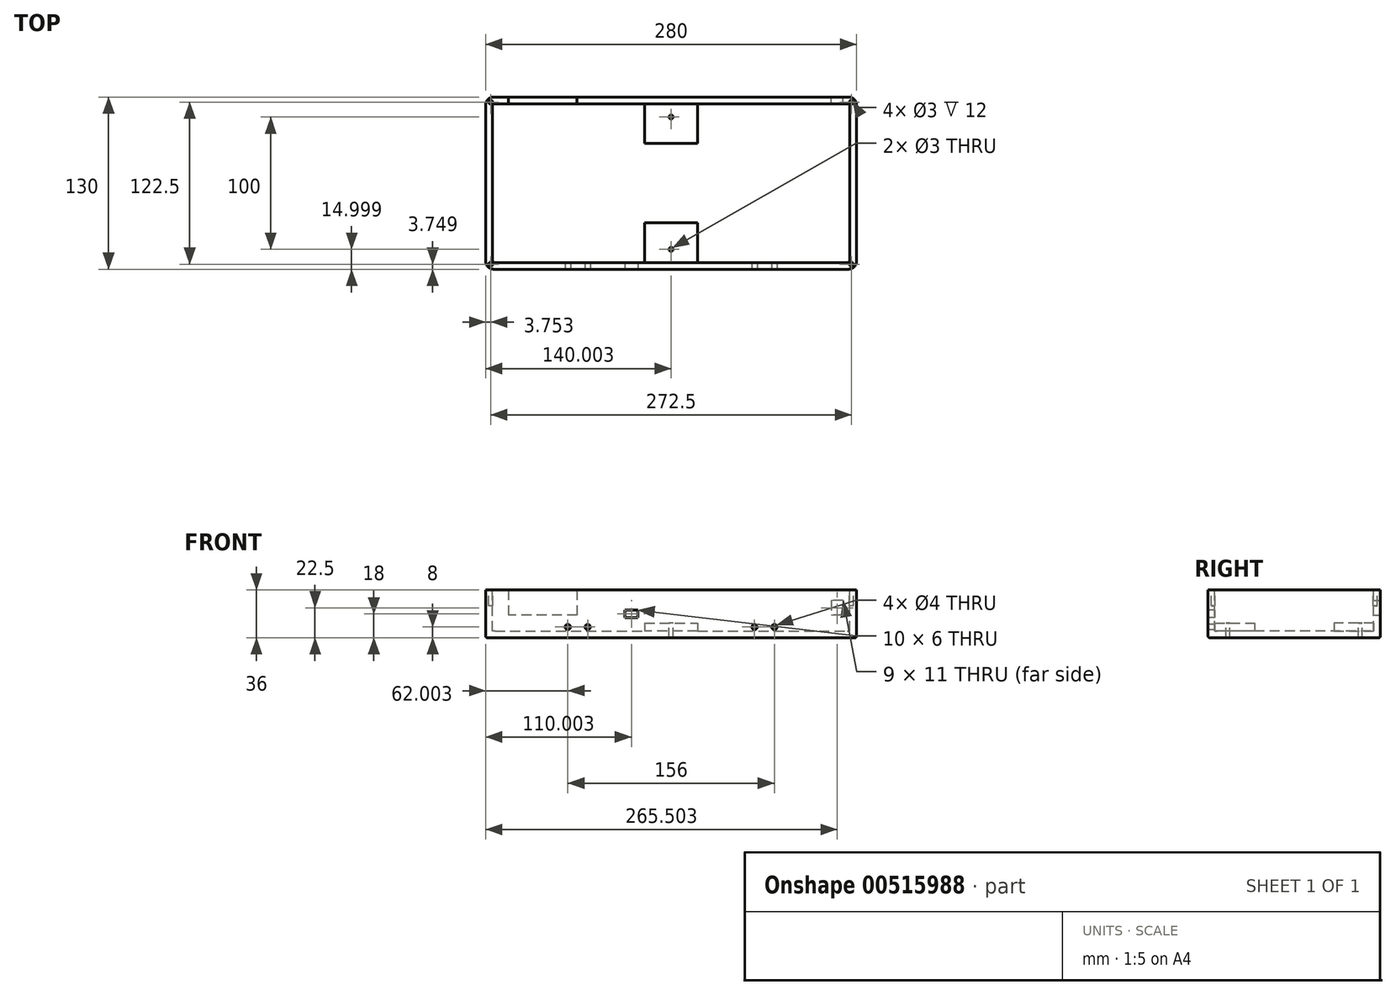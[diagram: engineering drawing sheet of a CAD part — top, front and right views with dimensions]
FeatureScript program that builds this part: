
annotation { "Feature Type Name" : "Feature", "Feature Type Description" : "" }
export const myFeature = defineFeature(function(context is Context, id is Id, definition is map)
    precondition{}
    {
        {
            var Q0;
            Q0=qCreatedBy(makeId("Top.planeOp"),FACE);
            var sketch = newSketch(context, id + "F0", { "sketchPlane" : qUnion([Q0])});
            skLineSegment(sketch, "E0.bottom", {"start": v(-152.6, 53.73) * mm, "end": v(127.4, 53.73) * mm});
            skLineSegment(sketch, "E0.top", {"start": v(-152.6, -76.27) * mm, "end": v(127.4, -76.27) * mm});
            skLineSegment(sketch, "E0.left", {"start": v(-152.6, 53.73) * mm, "end": v(-152.6, -76.27) * mm});
            skLineSegment(sketch, "E0.right", {"start": v(127.4, 53.73) * mm, "end": v(127.4, -76.27) * mm});
            skSolve(sketch);
        }
        {
            var Q0;
            Q0=makeQuery(id+"F0.imprint","IMPRINT",FACE,{"disambiguationData":[TD([[makeQuery(id+"F0.imprint","IMPRINT",EDGE,{"derivedFrom":sQuery(id+"F0.wireOp",EDGE,"E0.bottom")}),-1.0]])]});
            extrude(context, id + "F1", {"entities" : qUnion([Q0]), "depth" : 36 * mm, "offsetDistance" : 25 * mm});
        }
        {
            var Q0;
            Q0=makeQuery(id+"F1.opExtrude","CAP_FACE",FACE,{"disambiguationData":[OSD([sQuery(id+"F0.wireOp",EDGE,"E0.bottom"),sQuery(id+"F0.wireOp",EDGE,"E0.top"),sQuery(id+"F0.wireOp",EDGE,"E0.left"),sQuery(id+"F0.wireOp",EDGE,"E0.right")])],"isStart":false});
            var sketch = newSketch(context, id + "F2", { "sketchPlane" : qUnion([Q0])});
            skLineSegment(sketch, "E1.bottom", {"start": v(-147.6, 48.73) * mm, "end": v(122.4, 48.73) * mm});
            skLineSegment(sketch, "E1.top", {"start": v(-147.6, -71.27) * mm, "end": v(122.4, -71.27) * mm});
            skLineSegment(sketch, "E1.left", {"start": v(-147.6, 48.73) * mm, "end": v(-147.6, -71.27) * mm});
            skLineSegment(sketch, "E1.right", {"start": v(122.4, 48.73) * mm, "end": v(122.4, -71.27) * mm});
            skSolve(sketch);
        }
        {
            var Q0;
            Q0=makeQuery(id+"F2.imprint","IMPRINT",FACE,{"disambiguationData":[TD([[makeQuery(id+"F2.imprint","IMPRINT",EDGE,{"derivedFrom":sQuery(id+"F2.wireOp",EDGE,"E1.bottom")}),-1.0]])]});
            extrude(context, id + "F3", {"entities" : qUnion([Q0]), "operationType" : NewBodyOperationType.REMOVE, "oppositeDirection" : true, "depth" : 31 * mm, "offsetDistance" : 25 * mm});
        }
        {
            var Q0;
            Q0=makeQuery(id+"F1.opExtrude","SWEPT_FACE",FACE,{"disambiguationData":[OSD([sQuery(id+"F0.wireOp",EDGE,"E0.top")])]});
            var sketch = newSketch(context, id + "F4", { "sketchPlane" : qUnion([Q0])});
            skCircle(sketch, "E2", {"center": v(-90.6, 8) * mm, "radius": 2 * mm});
            skCircle(sketch, "E3", {"center": v(-75.6, 8) * mm, "radius": 2 * mm});
            skCircle(sketch, "E4", {"center": v(50.4, 8) * mm, "radius": 2 * mm});
            skCircle(sketch, "E5", {"center": v(65.4, 8) * mm, "radius": 2 * mm});
            skLineSegment(sketch, "E6.bottom", {"start": v(-47.6, 21) * mm, "end": v(-37.6, 21) * mm});
            skLineSegment(sketch, "E6.top", {"start": v(-47.6, 15) * mm, "end": v(-37.6, 15) * mm});
            skLineSegment(sketch, "E6.left", {"start": v(-47.6, 21) * mm, "end": v(-47.6, 15) * mm});
            skLineSegment(sketch, "E6.right", {"start": v(-37.6, 21) * mm, "end": v(-37.6, 15) * mm});
            skSolve(sketch);
        }
        {
            var Q0;
            Q0=makeQuery(id+"F1.opExtrude","SWEPT_FACE",FACE,{"disambiguationData":[OSD([sQuery(id+"F0.wireOp",EDGE,"E0.bottom")])]});
            var sketch = newSketch(context, id + "F5", { "sketchPlane" : qUnion([Q0])});
            skLineSegment(sketch, "E7.bottom", {"start": v(83.6, 36) * mm, "end": v(135.6, 36) * mm});
            skLineSegment(sketch, "E7.top", {"start": v(83.6, 17) * mm, "end": v(135.6, 17) * mm});
            skLineSegment(sketch, "E7.left", {"start": v(83.6, 36) * mm, "end": v(83.6, 17) * mm});
            skLineSegment(sketch, "E7.right", {"start": v(135.6, 36) * mm, "end": v(135.6, 17) * mm});
            skLineSegment(sketch, "E8.bottom", {"start": v(-117.4, 28) * mm, "end": v(-108.4, 28) * mm});
            skLineSegment(sketch, "E8.top", {"start": v(-117.4, 17) * mm, "end": v(-108.4, 17) * mm});
            skLineSegment(sketch, "E8.left", {"start": v(-117.4, 28) * mm, "end": v(-117.4, 17) * mm});
            skLineSegment(sketch, "E8.right", {"start": v(-108.4, 28) * mm, "end": v(-108.4, 17) * mm});
            skSolve(sketch);
        }
        {
            var Q0;
            Q0=makeQuery(id+"F4.imprint","IMPRINT",FACE,{"disambiguationData":[TD([[makeQuery(id+"F4.imprint","IMPRINT",EDGE,{"derivedFrom":sQuery(id+"F4.wireOp",EDGE,"E2")}),1.0]])]});
            var Q1;
            Q1=makeQuery(id+"F4.imprint","IMPRINT",FACE,{"disambiguationData":[TD([[makeQuery(id+"F4.imprint","IMPRINT",EDGE,{"derivedFrom":sQuery(id+"F4.wireOp",EDGE,"E3")}),1.0]])]});
            var Q2;
            Q2=makeQuery(id+"F4.imprint","IMPRINT",FACE,{"disambiguationData":[TD([[makeQuery(id+"F4.imprint","IMPRINT",EDGE,{"derivedFrom":sQuery(id+"F4.wireOp",EDGE,"E4")}),1.0]])]});
            var Q3;
            Q3=makeQuery(id+"F4.imprint","IMPRINT",FACE,{"disambiguationData":[TD([[makeQuery(id+"F4.imprint","IMPRINT",EDGE,{"derivedFrom":sQuery(id+"F4.wireOp",EDGE,"E5")}),1.0]])]});
            var Q4;
            Q4=makeQuery(id+"F4.imprint","IMPRINT",FACE,{"disambiguationData":[TD([[makeQuery(id+"F4.imprint","IMPRINT",EDGE,{"derivedFrom":sQuery(id+"F4.wireOp",EDGE,"EG82mpZ8-gIm3-i3lA-bKAT-wHgxzZ3Zt91a")}),1.0]])]});
            var Q5;
            Q5=makeQuery(id+"F4.imprint","IMPRINT",FACE,{"disambiguationData":[TD([[makeQuery(id+"F4.imprint","IMPRINT",EDGE,{"derivedFrom":sQuery(id+"F4.wireOp",EDGE,"E6.bottom")}),-1.0]])]});
            extrude(context, id + "F6", {"entities" : qUnion([Q0, Q1, Q2, Q3, Q4, Q5]), "operationType" : NewBodyOperationType.REMOVE, "oppositeDirection" : true, "depth" : 25 * mm, "offsetDistance" : 25 * mm});
        }
        {
            var Q0;
            Q0=makeQuery(id+"F5.imprint","IMPRINT",FACE,{"disambiguationData":[TD([[makeQuery(id+"F5.imprint","IMPRINT",EDGE,{"derivedFrom":sQuery(id+"F5.wireOp",EDGE,"E7.bottom")}),-1.0]])]});
            var Q1;
            Q1=makeQuery(id+"F5.imprint","IMPRINT",FACE,{"disambiguationData":[TD([[makeQuery(id+"F5.imprint","IMPRINT",EDGE,{"derivedFrom":sQuery(id+"F5.wireOp",EDGE,"E8.bottom")}),-1.0]])]});
            var Q2;
            Q2=makeQuery(id+"F5.imprint","IMPRINT",FACE,{"disambiguationData":[TD([[makeQuery(id+"F5.imprint","IMPRINT",EDGE,{"derivedFrom":sQuery(id+"F5.wireOp",EDGE,"E7.bottom")}),1.0]])]});
            extrude(context, id + "F7", {"entities" : qUnion([Q0, Q1, Q2]), "operationType" : NewBodyOperationType.REMOVE, "oppositeDirection" : true, "depth" : 25 * mm, "offsetDistance" : 25 * mm});
        }
        {
            var Q0;
            Q0=makeQuery(id+"F1.opExtrude","CAP_FACE",FACE,{"disambiguationData":[OSD([sQuery(id+"F0.wireOp",EDGE,"E0.bottom"),sQuery(id+"F0.wireOp",EDGE,"E0.top"),sQuery(id+"F0.wireOp",EDGE,"E0.left"),sQuery(id+"F0.wireOp",EDGE,"E0.right")])],"isStart":true});
            var sketch = newSketch(context, id + "F8", { "sketchPlane" : qUnion([Q0])});
            skLineSegment(sketch, "E9.bottom", {"start": v(-32.6, 71.27) * mm, "end": v(7.4, 71.27) * mm});
            skLineSegment(sketch, "E9.top", {"start": v(-32.6, 41.27) * mm, "end": v(7.4, 41.27) * mm});
            skLineSegment(sketch, "E9.left", {"start": v(-32.6, 71.27) * mm, "end": v(-32.6, 41.27) * mm});
            skLineSegment(sketch, "E9.right", {"start": v(7.4, 71.27) * mm, "end": v(7.4, 41.27) * mm});
            skLineSegment(sketch, "E10.bottom", {"start": v(-32.6, -48.73) * mm, "end": v(7.4, -48.73) * mm});
            skLineSegment(sketch, "E10.top", {"start": v(-32.6, -18.73) * mm, "end": v(7.4, -18.73) * mm});
            skLineSegment(sketch, "E10.left", {"start": v(-32.6, -48.73) * mm, "end": v(-32.6, -18.73) * mm});
            skLineSegment(sketch, "E10.right", {"start": v(7.4, -48.73) * mm, "end": v(7.4, -18.73) * mm});
            skSolve(sketch);
        }
        {
            var Q0;
            Q0=makeQuery(id+"F8.imprint","IMPRINT",FACE,{"disambiguationData":[TD([[makeQuery(id+"F8.imprint","IMPRINT",EDGE,{"derivedFrom":sQuery(id+"F8.wireOp",EDGE,"oHtQnYNI-7E0c-D78Y-z765-Ff1MrF6Kfo6s")}),1.0]])]});
            var Q1;
            Q1=makeQuery(id+"F8.imprint","IMPRINT",FACE,{"disambiguationData":[TD([[makeQuery(id+"F8.imprint","IMPRINT",EDGE,{"derivedFrom":sQuery(id+"F8.wireOp",EDGE,"WgwQHs1F-avJm-uaX9-2PcI-Fn2cRxu6mppU")}),1.0]])]});
            var Q2;
            Q2=makeQuery(id+"F8.imprint","IMPRINT",FACE,{"disambiguationData":[TD([[makeQuery(id+"F8.imprint","IMPRINT",EDGE,{"derivedFrom":sQuery(id+"F8.wireOp",EDGE,"E10.bottom")}),1.0]])]});
            var Q3;
            Q3=makeQuery(id+"F8.imprint","IMPRINT",FACE,{"disambiguationData":[TD([[makeQuery(id+"F8.imprint","IMPRINT",EDGE,{"derivedFrom":sQuery(id+"F8.wireOp",EDGE,"E9.bottom")}),-1.0]])]});
            var Q4;
            Q4=sQuery(id+"F8.wireOp",EDGE,"oHtQnYNI-7E0c-D78Y-z765-Ff1MrF6Kfo6s");
            var Q5;
            Q5=sQuery(id+"F8.wireOp",EDGE,"WgwQHs1F-avJm-uaX9-2PcI-Fn2cRxu6mppU");
            extrude(context, id + "F9", {"entities" : qUnion([Q0, Q1, Q2, Q3]), "operationType" : NewBodyOperationType.ADD, "surfaceEntities" : qUnion([Q4, Q5]), "oppositeDirection" : true, "depth" : 11 * mm, "offsetDistance" : 25 * mm});
        }
        {
            var Q0;
            Q0=makeQuery(id+"F9.opExtrude","CAP_FACE",FACE,{"disambiguationData":[OSD([sQuery(id+"F8.wireOp",EDGE,"E10.bottom"),sQuery(id+"F8.wireOp",EDGE,"E10.top"),sQuery(id+"F8.wireOp",EDGE,"E10.left"),sQuery(id+"F8.wireOp",EDGE,"E10.right")])],"isStart":false});
            var sketch = newSketch(context, id + "F10", { "sketchPlane" : qUnion([Q0])});
            skCircle(sketch, "E11", {"center": v(-12.6, 38.73) * mm, "radius": 1.5 * mm});
            skCircle(sketch, "E12", {"center": v(-12.6, -61.27) * mm, "radius": 1.5 * mm});
            skSolve(sketch);
        }
        {
            var Q0;
            Q0=makeQuery(id+"F10.imprint","IMPRINT",FACE,{"disambiguationData":[TD([[makeQuery(id+"F10.imprint","IMPRINT",EDGE,{"derivedFrom":sQuery(id+"F10.wireOp",EDGE,"E11")}),1.0]])]});
            var Q1;
            Q1=makeQuery(id+"F10.imprint","IMPRINT",FACE,{"disambiguationData":[TD([[makeQuery(id+"F10.imprint","IMPRINT",EDGE,{"derivedFrom":sQuery(id+"F10.wireOp",EDGE,"E12")}),1.0]])]});
            extrude(context, id + "F11", {"entities" : qUnion([Q0, Q1]), "operationType" : NewBodyOperationType.REMOVE, "oppositeDirection" : true, "depth" : 12 * mm, "offsetDistance" : 25 * mm});
        }
        {
            var Q0;
            Q0=makeQuery(id+"F1.opExtrude","CAP_FACE",FACE,{"disambiguationData":[OSD([sQuery(id+"F0.wireOp",EDGE,"E0.bottom"),sQuery(id+"F0.wireOp",EDGE,"E0.top"),sQuery(id+"F0.wireOp",EDGE,"E0.left"),sQuery(id+"F0.wireOp",EDGE,"E0.right")])],"isStart":false});
            var sketch = newSketch(context, id + "F12", { "sketchPlane" : qUnion([Q0])});
            skCircle(sketch, "E13", {"center": v(-148.85, 49.98) * mm, "radius": 1.5 * mm});
            skCircle(sketch, "E14", {"center": v(-148.85, -72.52) * mm, "radius": 1.5 * mm});
            skCircle(sketch, "E15", {"center": v(123.65, 49.98) * mm, "radius": 1.5 * mm});
            skCircle(sketch, "E16", {"center": v(123.65, -72.52) * mm, "radius": 1.5 * mm});
            skSolve(sketch);
        }
        {
            var Q0;
            Q0=makeQuery(id+"F12.imprint","IMPRINT",FACE,{"disambiguationData":[TD([[makeQuery(id+"F12.imprint","IMPRINT",EDGE,{"derivedFrom":sQuery(id+"F12.wireOp",EDGE,"E13")}),1.0]])]});
            var Q1;
            Q1=makeQuery(id+"F12.imprint","IMPRINT",FACE,{"disambiguationData":[TD([[makeQuery(id+"F12.imprint","IMPRINT",EDGE,{"derivedFrom":sQuery(id+"F12.wireOp",EDGE,"E14")}),1.0]])]});
            var Q2;
            Q2=makeQuery(id+"F12.imprint","IMPRINT",FACE,{"disambiguationData":[TD([[makeQuery(id+"F12.imprint","IMPRINT",EDGE,{"derivedFrom":sQuery(id+"F12.wireOp",EDGE,"E16")}),1.0]])]});
            var Q3;
            Q3=makeQuery(id+"F12.imprint","IMPRINT",FACE,{"disambiguationData":[TD([[makeQuery(id+"F12.imprint","IMPRINT",EDGE,{"derivedFrom":sQuery(id+"F12.wireOp",EDGE,"E15")}),1.0]])]});
            extrude(context, id + "F13", {"entities" : qUnion([Q0, Q1, Q2, Q3]), "operationType" : NewBodyOperationType.REMOVE, "oppositeDirection" : true, "depth" : 12 * mm, "offsetDistance" : 25 * mm});
        }
        {
            var Q0;
            Q0=makeQuery(id+"F1.opExtrude","SWEPT_EDGE",EDGE,{"disambiguationData":[OSD([sQuery(id+"F0.wireOp",EDGE,"E0.top"),sQuery(id+"F0.wireOp",EDGE,"E0.left")])]});
            var Q1;
            Q1=makeQuery(id+"F1.opExtrude","SWEPT_EDGE",EDGE,{"disambiguationData":[OSD([sQuery(id+"F0.wireOp",EDGE,"E0.bottom"),sQuery(id+"F0.wireOp",EDGE,"E0.left")])]});
            var Q2;
            Q2=makeQuery(id+"F1.opExtrude","SWEPT_EDGE",EDGE,{"disambiguationData":[OSD([sQuery(id+"F0.wireOp",EDGE,"E0.top"),sQuery(id+"F0.wireOp",EDGE,"E0.right")])]});
            var Q3;
            Q3=makeQuery(id+"F1.opExtrude","SWEPT_EDGE",EDGE,{"disambiguationData":[OSD([sQuery(id+"F0.wireOp",EDGE,"E0.bottom"),sQuery(id+"F0.wireOp",EDGE,"E0.right")])]});
            fillet(context, id + "F14", {"entities" : qUnion([Q0, Q1, Q2, Q3]), "radius" : 6 * mm, "tangentPropagation" : true, "allowEdgeOverflow" : false});
        }
        {
            var Q0;
            Q0=makeQuery(id+"F3.boolean.opBoolean","COPY",EDGE,{"derivedFrom":makeQuery(id+"F3.opExtrude","SWEPT_EDGE",EDGE,{"disambiguationData":[OSD([sQuery(id+"F2.wireOp",EDGE,"E1.bottom"),sQuery(id+"F2.wireOp",EDGE,"E1.left")])]})});
            var Q1;
            Q1=makeQuery(id+"F3.boolean.opBoolean","COPY",EDGE,{"derivedFrom":makeQuery(id+"F3.opExtrude","SWEPT_EDGE",EDGE,{"disambiguationData":[OSD([sQuery(id+"F2.wireOp",EDGE,"E1.top"),sQuery(id+"F2.wireOp",EDGE,"E1.left")])]})});
            var Q2;
            Q2=makeQuery(id+"F3.boolean.opBoolean","COPY",EDGE,{"derivedFrom":makeQuery(id+"F3.opExtrude","SWEPT_EDGE",EDGE,{"disambiguationData":[OSD([sQuery(id+"F2.wireOp",EDGE,"E1.bottom"),sQuery(id+"F2.wireOp",EDGE,"E1.right")])]})});
            var Q3;
            Q3=makeQuery(id+"F3.boolean.opBoolean","COPY",EDGE,{"derivedFrom":makeQuery(id+"F3.opExtrude","SWEPT_EDGE",EDGE,{"disambiguationData":[OSD([sQuery(id+"F2.wireOp",EDGE,"E1.top"),sQuery(id+"F2.wireOp",EDGE,"E1.right")])]})});
            fillet(context, id + "F15", {"entities" : qUnion([Q0, Q1, Q2, Q3]), "radius" : 2 * mm, "tangentPropagation" : true, "allowEdgeOverflow" : false});
        }
        {
            var Q0;
            Q0=makeQuery(id+"F1.opExtrude","CAP_EDGE",EDGE,{"disambiguationData":[OSD([sQuery(id+"F0.wireOp",EDGE,"E0.left")])],"isStart":true});
            fillet(context, id + "F16", {"entities" : qUnion([Q0]), "radius" : 1 * mm, "tangentPropagation" : true, "allowEdgeOverflow" : false});
        }
    });
